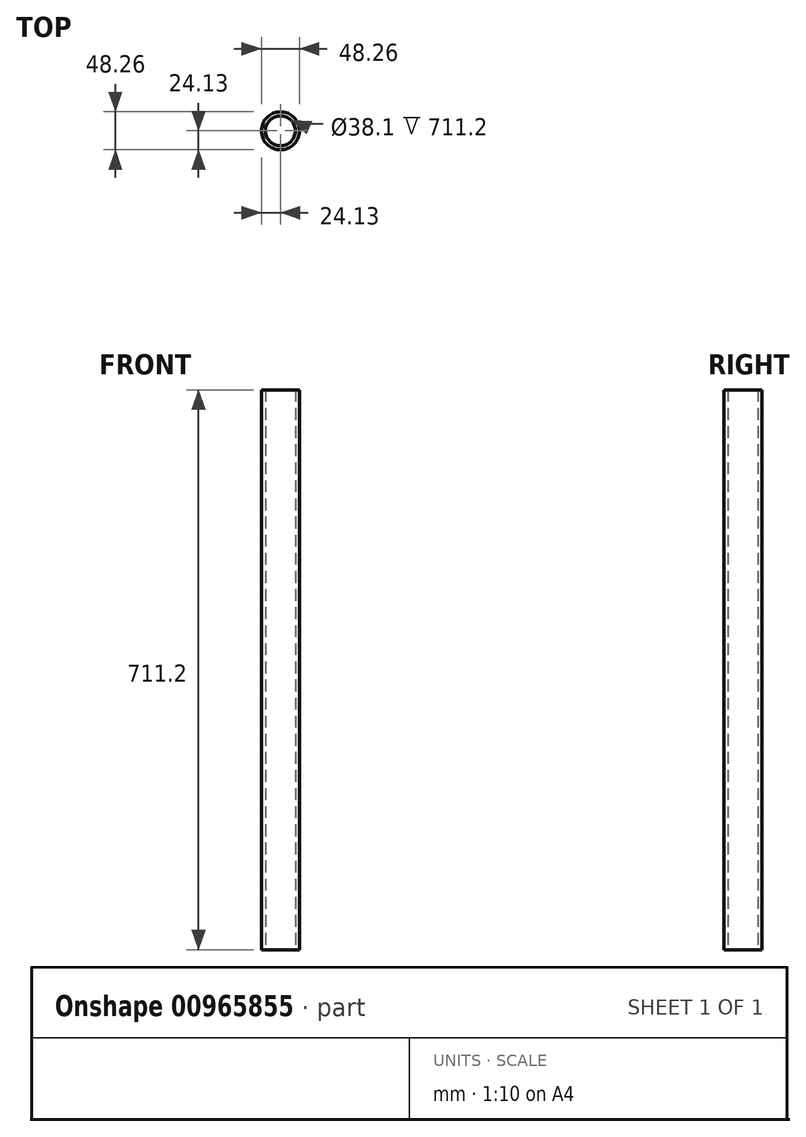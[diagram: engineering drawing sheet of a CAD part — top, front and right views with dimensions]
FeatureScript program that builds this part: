
annotation { "Feature Type Name" : "Feature", "Feature Type Description" : "" }
export const myFeature = defineFeature(function(context is Context, id is Id, definition is map)
    precondition{}
    {
        {
            var Q0;
            Q0=qCreatedBy(makeId("Top.planeOp"),FACE);
            var sketch = newSketch(context, id + "F0", { "sketchPlane" : qUnion([Q0])});
            skCircle(sketch, "E0", {"center": v(0, 0) * mm, "radius": 24.13 * mm});
            skCircle(sketch, "E1", {"center": v(0, 0) * mm, "radius": 19.05 * mm});
            skSolve(sketch);
        }
        {
            var Q0;
            Q0=makeQuery(id+"F0.imprint","IMPRINT",FACE,{"disambiguationData":[TD([[makeQuery(id+"F0.imprint","IMPRINT",EDGE,{"derivedFrom":sQuery(id+"F0.wireOp",EDGE,"E0")}),1.0]])]});
            extrude(context, id + "F1", {"entities" : qUnion([Q0]), "depth" : 711.2 * mm, "offsetDistance" : 25.4 * mm});
        }
    });
